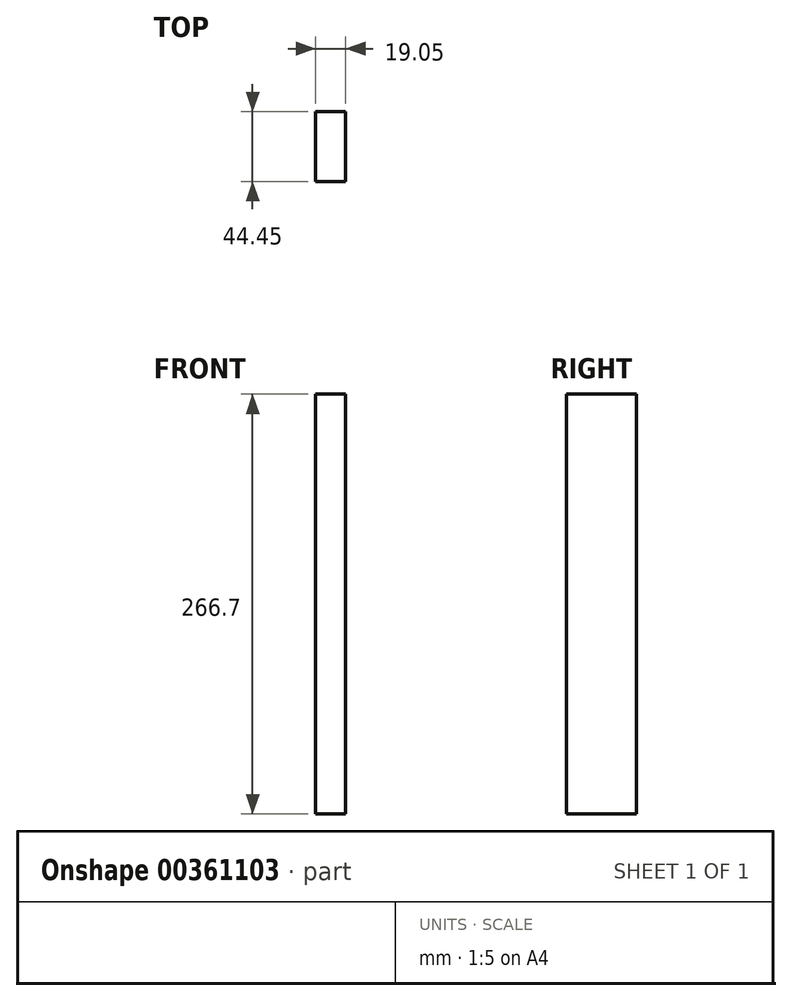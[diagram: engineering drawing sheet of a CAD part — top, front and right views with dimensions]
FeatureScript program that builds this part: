
annotation { "Feature Type Name" : "Feature", "Feature Type Description" : "" }
export const myFeature = defineFeature(function(context is Context, id is Id, definition is map)
    precondition{}
    {
        {
            var Q0;
            Q0=qCreatedBy(makeId("Right.planeOp"),FACE);
            var sketch = newSketch(context, id + "F0", { "sketchPlane" : qUnion([Q0])});
            skLineSegment(sketch, "E0.bottom", {"start": v(-115.08, 121.38) * mm, "end": v(-70.63, 121.38) * mm});
            skLineSegment(sketch, "E0.top", {"start": v(-115.08, -145.32) * mm, "end": v(-70.63, -145.32) * mm});
            skLineSegment(sketch, "E0.left", {"start": v(-115.08, 121.38) * mm, "end": v(-115.08, -145.32) * mm});
            skLineSegment(sketch, "E0.right", {"start": v(-70.63, 121.38) * mm, "end": v(-70.63, -145.32) * mm});
            skSolve(sketch);
        }
        {
            var Q0;
            Q0=qSketchRegion(id+"F0",true);
            extrude(context, id + "F1", {"entities" : qUnion([Q0]), "depth" : 19.05 * mm});
        }
    });
